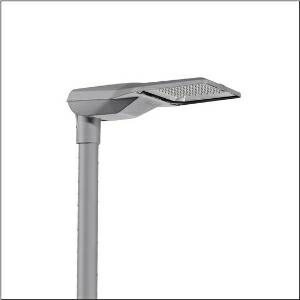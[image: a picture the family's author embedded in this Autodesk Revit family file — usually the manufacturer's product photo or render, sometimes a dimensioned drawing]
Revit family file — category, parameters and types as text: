
# Revit family: streetlight_sl_21_iq_midi___stw1_0a_5xe3e31g08mb_59a2
name_source: partatom
category: Lighting Fixtures
units: mm (PartAtom-declared; Revit-internal decimal feet)

## family parameters
Cut with Voids When Loaded = No
Host = Face
Light Source = No
Part Type = Normal
Room Calculation Point = No
Round Connector Dimension = Use Diameter
Shared = No

## types (1)
- --- (1 x LED, 19500 lm, 146.7 W, 3000K)
    Apparent Load = 147 VA
    CIE Flux Codes = 38 75 98 100 100
    Color Rendering = 70
    Color Temperature = 3000K
    Default Elevation = 1800 mm
    Description = Streetlight SL 21 iQ midi, mast luminaire, primary light control with lens, of PMMA, primary optical cover: cover, of toughened safety glass, transparent, light distribution: STW1.0a, light emission: direct distribution, primary light characteristic: asymmetric, installation type: post-top, side-entry, LED, High Power LED, rated luminous flux: 19.500lm, luminous efficacy: 133lm/W, light colour: 730, colour temperature: 3000K, control gear: iQ Street-Remote, control: Street-Remote, Auto-Match, Temp-Guard, Lumen-Switch, Night-Set, Smart-Wire, Light-Fading, Desk-Remote (wireless, voltage-free reading and setting of iQ features in the workshop via application-optimized NFC function/RFID function), optimised constant luminous flux control (CLO 2.0), pre-setting: linear dimming characteristic, mains connection: 230..240V, AC, 50/60Hz, start of lifetime: 147W, end of service life: 161W, reduction: 62W, luminaire housing, of diecast aluminium, powder-coated, SITECO metallic grey (DB 702S), corrosivity category C5 high according to DIN EN ISO 12944, please order mast flange separately, inclination adjustable: 0°, 5°, 10°, 15°, sealing non-destructively replaceable, multi-level sealing system, length: 644mm, width: 335mm, height: 110mm, mast flange for spigot size: 42mm (side-entry): 5XC10008XM4, 60/48mm (side-entry/post-top): 5XC10108XM2, 76/60mm (side-entry/post-top): 5XC10108XM1, mounting height: 4..8m, protection rating (complete): IP66, insulation class (complete): insulation class II (safety insulation), certification: CE, ENEC, ENEC+, VDE, impact resistance: IK10, permissible operating ambient temperature for outdoor applications: -40..+50°C, standard-compliant lighting for roads and squares, packaging unit: 1 piece

Light Distribution: STW1.0a
    Height = 111 mm
    Lamp = 1 x LED
    Lamp Light Flux = 19500 lm
    Lamp Power = 146.7 W
    Lamp count = 1
    Length = 644 mm
    Luminous efficacy = 133 lm/W
    Manufacturer = Siteco
    ModVariant = No
    Model = 5XE3E31G08MB
    Number of Poles = 1
    OnlyDefault = Yes
    Power Factor = 1
    Product Name = Streetlight SL 21 iQ midi | STW1.0a
    Product group = mast luminaire | pylon top
    ProductGroupID = 6100
    Protection Class = Protection class II
    Protection Degree = IP 66
    RLX_Detail_Level = 1
    RLX_Emergency_Light_Flux = 0 lm
    RLX_Emergency_Type = 0
    RLX_Emergency_Type_DB = No
    RlxData = <blob elided: 26985 chars, md5=aac6e8de>
    Socket = socket
    Standby Power = 0 W
    System Light Flux = 19499 lm
    System Power = 147 W
    Type Comments = factory setting: luminous flux: 100 % | dim-lin: 254 | 753 mA
    Type Image = l_1004298.jpg
    URL = http://relux.com
    VarID = @adj_185563
    Voltage = 0 V
    Weight = 0.00 kg
    Width = 336 mm

## geometry (parser evidence)
native form markers: Blend x4, Sweep x11
no freeform markers — native parametric forms only
